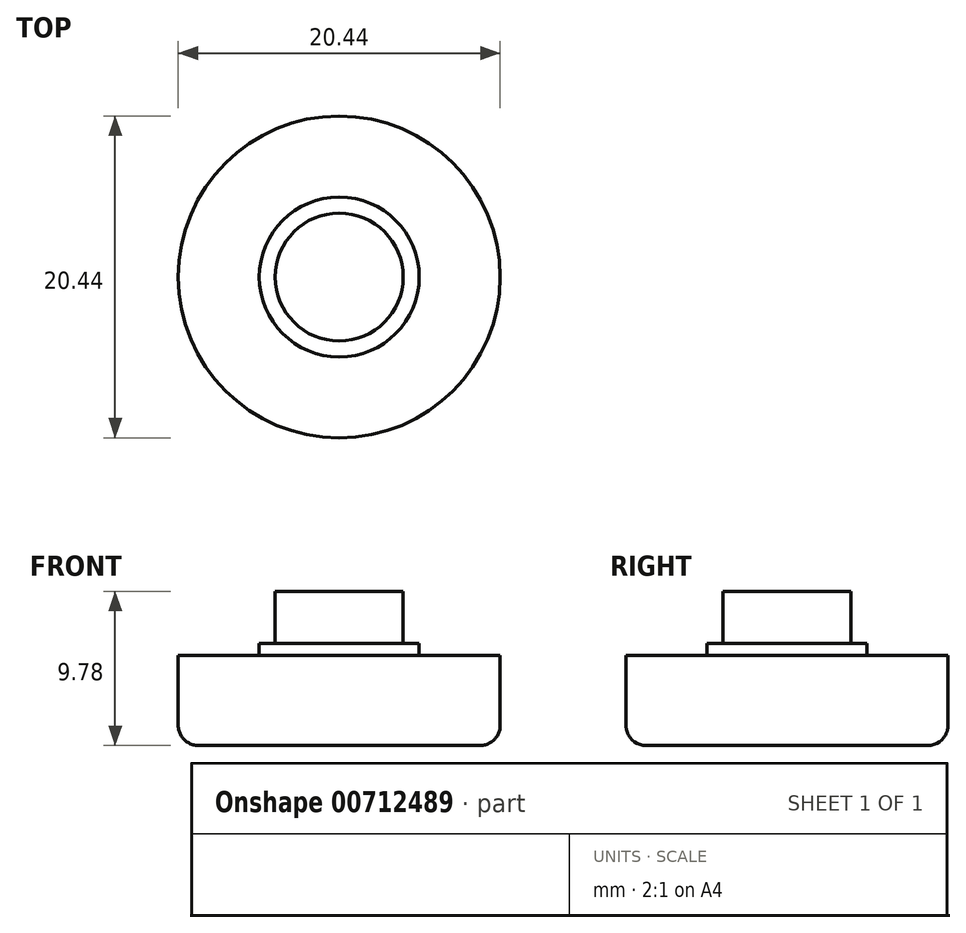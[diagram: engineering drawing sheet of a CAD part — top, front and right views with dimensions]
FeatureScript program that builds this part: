
annotation { "Feature Type Name" : "Feature", "Feature Type Description" : "" }
export const myFeature = defineFeature(function(context is Context, id is Id, definition is map)
    precondition{}
    {
        {
            var Q0;
            Q0=qCreatedBy(makeId("Top.planeOp"),FACE);
            var sketch = newSketch(context, id + "F0", { "sketchPlane" : qUnion([Q0])});
            skCircle(sketch, "E0", {"center": v(0, 0) * mm, "radius": 10.22 * mm});
            skSolve(sketch);
        }
        {
            var Q0;
            Q0=qCreatedBy(makeId("Top.planeOp"),FACE);
            var sketch = newSketch(context, id + "F1", { "sketchPlane" : qUnion([Q0])});
            skCircle(sketch, "E1", {"center": v(0, 0) * mm, "radius": 5.08 * mm});
            skSolve(sketch);
        }
        {
            var Q0;
            Q0=qCreatedBy(makeId("Top.planeOp"),FACE);
            var sketch = newSketch(context, id + "F2", { "sketchPlane" : qUnion([Q0])});
            skCircle(sketch, "E2", {"center": v(0, 0) * mm, "radius": 4.06 * mm});
            skSolve(sketch);
        }
        {
            var Q0;
            Q0 = qSketchRegion(id + "F0", true);
            extrude(context, id + "F3", {"entities" : qUnion([Q0]), "depth" : 5.7 * mm, "offsetDistance" : 25.4 * mm});
        }
        {
            var Q0;
            Q0 = qSketchRegion(id + "F1", true);
            extrude(context, id + "F4", {"entities" : qUnion([Q0]), "operationType" : NewBodyOperationType.ADD, "depth" : 6.48 * mm, "offsetDistance" : 25.4 * mm});
        }
        {
            var Q0;
            Q0 = qSketchRegion(id + "F2", true);
            extrude(context, id + "F5", {"entities" : qUnion([Q0]), "operationType" : NewBodyOperationType.ADD, "depth" : 9.78 * mm, "offsetDistance" : 25.4 * mm});
        }
        {
            var Q0;
            Q0=makeQuery(id+"F3.opExtrude","CAP_EDGE",EDGE,{"disambiguationData":[OSD([sQuery(id+"F0.wireOp",EDGE,"E0")])],"isStart":true});
            fillet(context, id + "F6", {"entities" : qUnion([Q0]), "radius" : 1.27 * mm, "tangentPropagation" : true, "allowEdgeOverflow" : false});
        }
    });
